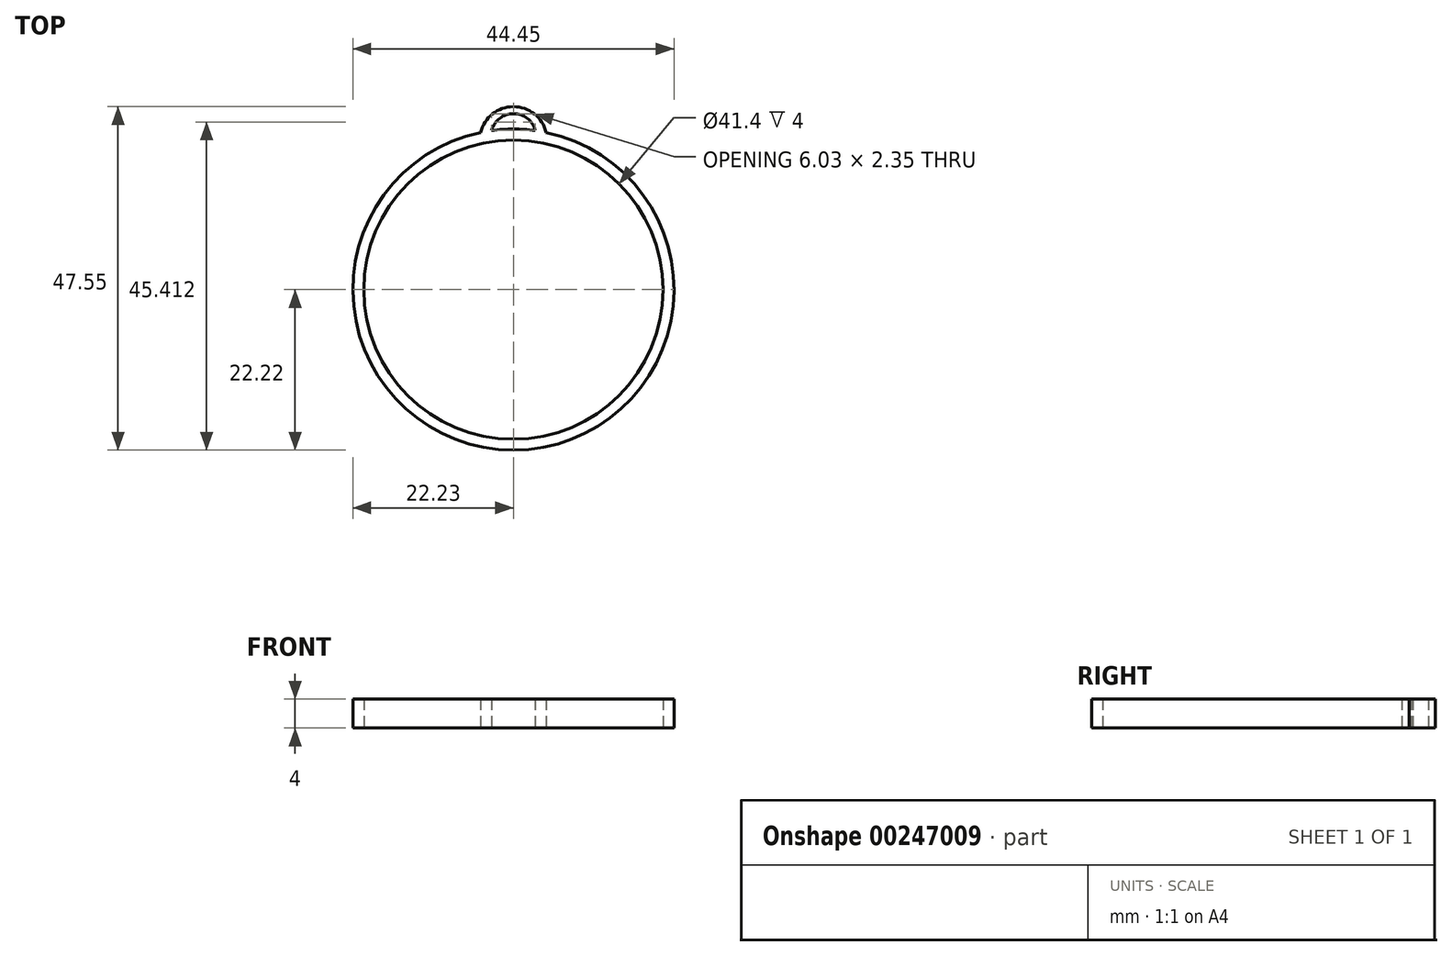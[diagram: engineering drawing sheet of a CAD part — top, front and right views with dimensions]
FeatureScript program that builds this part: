
annotation { "Feature Type Name" : "Feature", "Feature Type Description" : "" }
export const myFeature = defineFeature(function(context is Context, id is Id, definition is map)
    precondition{}
    {
        {
            var Q0;
            Q0=qCreatedBy(makeId("Top.planeOp"),FACE);
            var sketch = newSketch(context, id + "F0", { "sketchPlane" : qUnion([Q0])});
            skLineSegment(sketch, "E0.bottom", {"start": v(25.4, 25.4) * mm, "end": v(-25.4, 25.4) * mm});
            skLineSegment(sketch, "E0.top", {"start": v(25.4, -25.4) * mm, "end": v(-25.4, -25.4) * mm});
            skLineSegment(sketch, "E0.left", {"start": v(25.4, 25.4) * mm, "end": v(25.4, -25.4) * mm});
            skLineSegment(sketch, "E0.right", {"start": v(-25.4, 25.4) * mm, "end": v(-25.4, -25.4) * mm});
            skPoint(sketch, "E0.middle", {"position": v(0, 0) * mm});
            skCircle(sketch, "E1", {"center": v(0, 0) * mm, "radius": 22.23 * mm});
            skArc(sketch, "E2", {"start": v(4.54, 21.76) * mm, "mid": v(0, 25.33) * mm, "end": v(-4.54, 21.76) * mm});
            skArc(sketch, "E3", {"start": v(3.02, 22.02) * mm, "mid": v(0, 24.37) * mm, "end": v(-3.02, 22.02) * mm});
            skPoint(sketch, "E4", {"position": v(0, 24.37) * mm});
            skCircle(sketch, "E5", {"center": v(0, 0) * mm, "radius": 20.7 * mm});
            skSolve(sketch);
        }
        {
            var Q0;
            Q0=makeQuery(id+"F0.imprint","IMPRINT",FACE,{"disambiguationData":[TD([[makeQuery(id+"F0.imprint","IMPRINT",EDGE,{"derivedFrom":sQuery(id+"F0.wireOp",EDGE,"E5")}),-1.0]])]});
            var Q1;
            {var subQ0=sQuery(id+"F0.wireOp",EDGE,"E2");Q1=makeQuery(id+"F0.imprint","IMPRINT",FACE,{"disambiguationData":[TD([[makeQuery(id+"F0.imprint","IMPRINT",EDGE,{"derivedFrom":subQ0}),1.0]])]});}
            extrude(context, id + "F1", {"entities" : qUnion([Q0, Q1]), "depth" : 4 * mm});
        }
    });
